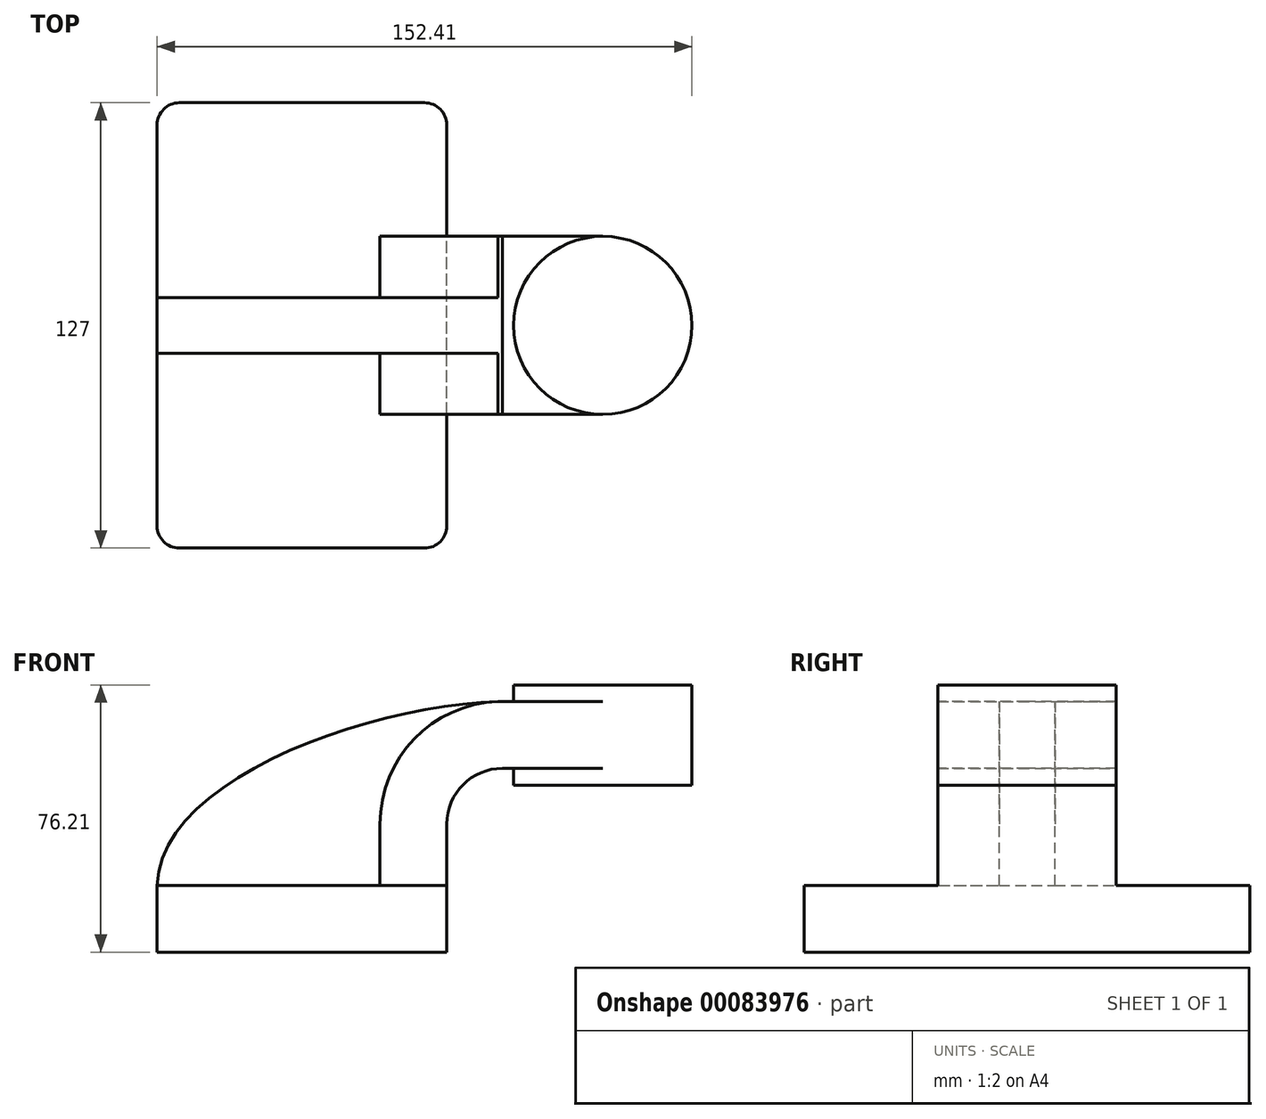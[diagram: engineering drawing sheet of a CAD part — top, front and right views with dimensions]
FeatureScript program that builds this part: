
annotation { "Feature Type Name" : "Feature", "Feature Type Description" : "" }
export const myFeature = defineFeature(function(context is Context, id is Id, definition is map)
    precondition{}
    {
        {
            var Q0;
            Q0=qCreatedBy(makeId("Front.planeOp"),FACE);
            var sketch = newSketch(context, id + "F0", { "sketchPlane" : qUnion([Q0])});
            skLineSegment(sketch, "E0.bottom", {"start": v(-41.28, 9.52) * mm, "end": v(41.27, 9.53) * mm});
            skLineSegment(sketch, "E0.top", {"start": v(-41.28, -9.52) * mm, "end": v(41.28, -9.52) * mm});
            skLineSegment(sketch, "E0.left", {"start": v(-41.28, 9.52) * mm, "end": v(-41.28, -9.53) * mm});
            skLineSegment(sketch, "E0.right", {"start": v(41.27, 9.53) * mm, "end": v(41.28, -9.52) * mm});
            skPoint(sketch, "E0.middle", {"position": v(0, 0) * mm});
            skLineSegment(sketch, "E1.bottom", {"start": v(60.32, 66.68) * mm, "end": v(111.12, 66.68) * mm});
            skLineSegment(sketch, "E1.top", {"start": v(60.32, 38.1) * mm, "end": v(111.12, 38.1) * mm});
            skLineSegment(sketch, "E1.left", {"start": v(60.32, 66.68) * mm, "end": v(60.32, 38.1) * mm});
            skLineSegment(sketch, "E1.right", {"start": v(111.12, 66.68) * mm, "end": v(111.12, 38.1) * mm});
            skPoint(sketch, "E1.middle", {"position": v(85.72, 52.39) * mm});
            skLineSegment(sketch, "E2", {"start": v(41.27, 9.53) * mm, "end": v(41.27, 27) * mm});
            skArc(sketch, "E3", {"start": v(41.27, 27) * mm, "mid": v(45.92, 38.23) * mm, "end": v(57.15, 42.88) * mm});
            skLineSegment(sketch, "E4", {"start": v(57.15, 42.88) * mm, "end": v(85.72, 42.88) * mm});
            skLineSegment(sketch, "E5.0", {"start": v(57.15, 61.93) * mm, "end": v(85.72, 61.93) * mm});
            skArc(sketch, "E5.1", {"start": v(22.22, 27) * mm, "mid": v(32.45, 51.7) * mm, "end": v(57.15, 61.93) * mm});
            skLineSegment(sketch, "E5.2", {"start": v(22.22, 9.53) * mm, "end": v(22.22, 27) * mm});
            skLineSegment(sketch, "E6", {"start": v(85.72, 38.1) * mm, "end": v(85.72, 61.93) * mm});
            skLineSegment(sketch, "E7", {"start": v(85.72, 38.1) * mm, "end": v(85.72, 66.68) * mm});
            skFitSpline(sketch, "E8", {"points": [v(-41.28, 9.53) * mm, v(57.15, 61.93) * mm], "startDerivative": vector(2.12, 91.78) * mm, "endDerivative": vector(109.19, 1.28) * mm});
            skSolve(sketch);
        }
        {
            var Q0;
            Q0=makeQuery(id+"F0.imprint","IMPRINT",FACE,{"disambiguationData":[TD([[makeQuery(id+"F0.imprint","IMPRINT",EDGE,{"derivedFrom":sQuery(id+"F0.wireOp",EDGE,"E0.top")}),1.0]])]});
            extrude(context, id + "F1", {"entities" : qUnion([Q0]), "endBound" : BoundingType.SYMMETRIC, "depth" : 127 * mm});
        }
        {
            var Q0;
            {var subQ1=sQuery(id+"F0.wireOp",EDGE,"E2");Q0=makeQuery(id+"F0.imprint","IMPRINT",FACE,{"disambiguationData":[TD([[makeQuery(id+"F0.imprint","IMPRINT",EDGE,{"derivedFrom":subQ1}),1.0]])]});}
            var Q1;
            {var subQ0=sQuery(id+"F0.wireOp",EDGE,"E5.0");var subQ1=sQuery(id+"F0.wireOp",EDGE,"E1.left");var subQ2=makeQuery(id+"F0.imprint","INTERSECT",VERTEX,{"derivedFrom":[subQ1,subQ0]});Q1=makeQuery(id+"F0.imprint","IMPRINT",FACE,{"disambiguationData":[TD([[makeQuery(id+"F0.imprint","IMPRINT",EDGE,{"disambiguationData":[TD([[subQ2,-1.0]])],"derivedFrom":subQ1}),1.0]])]});}
            extrude(context, id + "F2", {"entities" : qUnion([Q0, Q1]), "operationType" : NewBodyOperationType.ADD, "endBound" : BoundingType.SYMMETRIC, "depth" : 50.8 * mm});
        }
        {
            var Q0;
            {var subQ3=sQuery(id+"F0.wireOp",EDGE,"E5.2");Q0=makeQuery(id+"F0.imprint","IMPRINT",FACE,{"disambiguationData":[TD([[makeQuery(id+"F0.imprint","IMPRINT",EDGE,{"derivedFrom":subQ3}),1.0]])]});}
            extrude(context, id + "F3", {"entities" : qUnion([Q0]), "operationType" : NewBodyOperationType.ADD, "endBound" : BoundingType.SYMMETRIC, "depth" : 15.88 * mm});
        }
        {
            var Q0;
            {var subQ0=sQuery(id+"F0.wireOp",EDGE,"E1.right");Q0=makeQuery(id+"F0.imprint","IMPRINT",FACE,{"disambiguationData":[TD([[makeQuery(id+"F0.imprint","IMPRINT",EDGE,{"derivedFrom":subQ0}),-1.0]])]});}
            var Q1;
            Q1=sQuery(id+"F0.wireOp",EDGE,"E7");
            revolve(context, id + "F4", {"operationType" : NewBodyOperationType.ADD, "entities" : qUnion([Q0]), "axis" : qUnion([Q1]), "revolveType" : RevolveType.FULL});
        }
        {
            var Q0;
            Q0=makeQuery(id+"F1.opExtrude","CAP_EDGE",EDGE,{"disambiguationData":[OSD([sQuery(id+"F0.wireOp",EDGE,"E0.right")])],"isStart":false});
            var Q1;
            Q1=makeQuery(id+"F1.opExtrude","CAP_EDGE",EDGE,{"disambiguationData":[OSD([sQuery(id+"F0.wireOp",EDGE,"E0.left")])],"isStart":false});
            var Q2;
            Q2=makeQuery(id+"F1.opExtrude","CAP_EDGE",EDGE,{"disambiguationData":[OSD([sQuery(id+"F0.wireOp",EDGE,"E0.right")])],"isStart":true});
            var Q3;
            Q3=makeQuery(id+"F1.opExtrude","CAP_EDGE",EDGE,{"disambiguationData":[OSD([sQuery(id+"F0.wireOp",EDGE,"E0.left")])],"isStart":true});
            fillet(context, id + "F5", {"entities" : qUnion([Q0, Q1, Q2, Q3]), "radius" : 6.35 * mm, "tangentPropagation" : true, "allowEdgeOverflow" : false});
        }
    });
